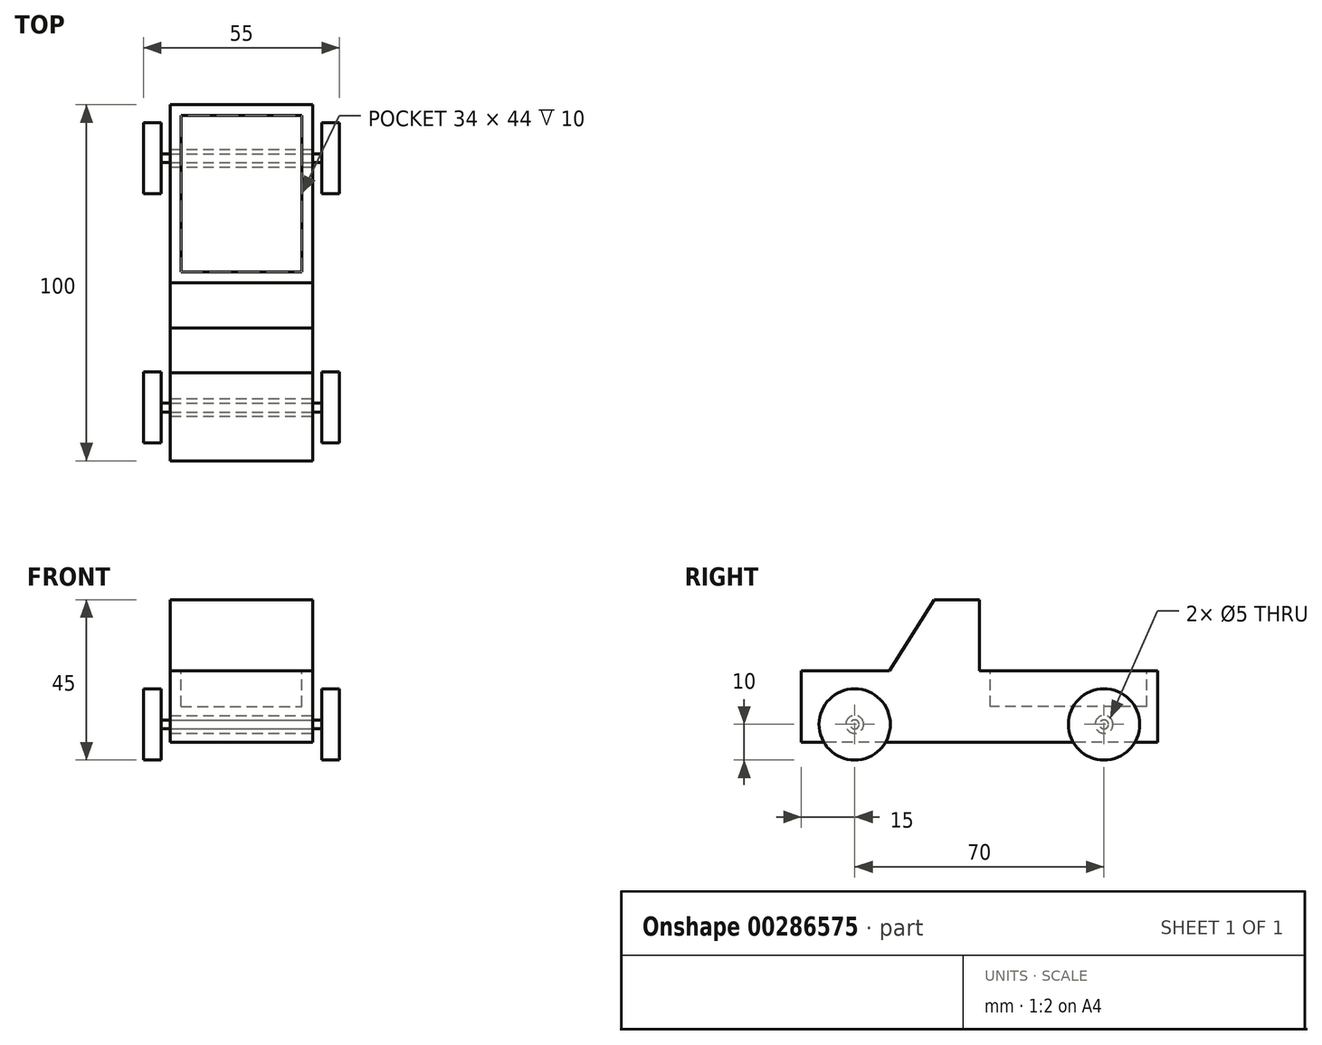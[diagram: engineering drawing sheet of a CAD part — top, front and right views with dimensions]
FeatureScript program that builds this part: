
annotation { "Feature Type Name" : "Feature", "Feature Type Description" : "" }
export const myFeature = defineFeature(function(context is Context, id is Id, definition is map)
    precondition{}
    {
        {
            var Q0;
            Q0=qCreatedBy(makeId("Right.planeOp"),FACE);
            var sketch = newSketch(context, id + "F0", { "sketchPlane" : qUnion([Q0])});
            skLineSegment(sketch, "E0.bottom", {"start": v(50, 10) * mm, "end": v(-50, 10) * mm});
            skLineSegment(sketch, "E0.top", {"start": v(50, -10) * mm, "end": v(-50, -10) * mm});
            skLineSegment(sketch, "E0.left", {"start": v(50, 10) * mm, "end": v(50, -10) * mm});
            skLineSegment(sketch, "E0.right", {"start": v(-50, 10) * mm, "end": v(-50, -10) * mm});
            skPoint(sketch, "E0.middle", {"position": v(0, 0) * mm});
            skSolve(sketch);
        }
        {
            var Q0;
            Q0 = qSketchRegion(id + "F0", true);
            extrude(context, id + "F1", {"entities" : qUnion([Q0]), "endBound" : BoundingType.SYMMETRIC, "depth" : 40 * mm});
        }
        {
            var Q0;
            Q0=makeQuery(id+"F1.opExtrude","SWEPT_FACE",FACE,{"disambiguationData":[OSD([sQuery(id+"F0.wireOp",EDGE,"E0.bottom")])]});
            var sketch = newSketch(context, id + "F2", { "sketchPlane" : qUnion([Q0])});
            skLineSegment(sketch, "E1", {"start": v(20, 0) * mm, "end": v(-20, 0) * mm});
            skSolve(sketch);
        }
        {
            var Q0;
            {var subQ0=sQuery(id+"F2.wireOp",EDGE,"E1");Q0=makeQuery(id+"F2.imprint","IMPRINT",FACE,{"disambiguationData":[TD([[makeQuery(id+"F2.imprint","IMPRINT",EDGE,{"derivedFrom":subQ0}),1.0]])]});}
            var sketch = newSketch(context, id + "F3", { "sketchPlane" : qUnion([Q0])});
            skLineSegment(sketch, "E2", {"start": v(-20, -25.3) * mm, "end": v(20, -25.3) * mm});
            skSolve(sketch);
        }
        {
            var Q0;
            {var subQ0=sQuery(id+"F3.wireOp",EDGE,"E2");Q0=makeQuery(id+"F3.imprint","IMPRINT",FACE,{"disambiguationData":[TD([[makeQuery(id+"F3.imprint","IMPRINT",EDGE,{"derivedFrom":subQ0}),1.0]])]});}
            var sketch = newSketch(context, id + "F4", { "sketchPlane" : qUnion([Q0])});
            skSolve(sketch);
        }
        {
            var Q0;
            Q0 = qSketchRegion(id + "F4", true);
            var Q1;
            {var subQ0=sQuery(id+"F3.wireOp",EDGE,"E2");Q1=makeQuery(id+"F4.imprint","IMPRINT",FACE,{"disambiguationData":[TD([[makeQuery(id+"F4.imprint","IMPRINT",EDGE,{"derivedFrom":makeQuery(id+"F3.imprint","IMPRINT",EDGE,{"derivedFrom":subQ0})}),1.0]])]});}
            extrude(context, id + "F5", {"entities" : qUnion([Q0, Q1]), "operationType" : NewBodyOperationType.ADD, "depth" : 20 * mm});
        }
        {
            var Q0;
            Q0=makeQuery(id+"F5.opExtrude","CAP_FACE",FACE,{"disambiguationData":[OSD([sQuery(id+"F0.wireOp",EDGE,"E0.bottom"),sQuery(id+"F2.wireOp",EDGE,"E1"),sQuery(id+"F3.wireOp",EDGE,"E2")])],"isStart":false});
            var sketch = newSketch(context, id + "F6", { "sketchPlane" : qUnion([Q0])});
            skLineSegment(sketch, "E3", {"start": v(-20, -15) * mm, "end": v(20, -15) * mm});
            skSolve(sketch);
        }
        {
            var Q0;
            {var subQ0=sQuery(id+"F0.wireOp",EDGE,"E0.bottom");var subQ1=makeQuery(id+"F1.opExtrude","CAP_EDGE",EDGE,{"disambiguationData":[OSD([subQ0])],"isStart":false});var subQ2=sQuery(id+"F0.wireOp",EDGE,"E0.right");var subQ3=sQuery(id+"F2.wireOp",EDGE,"E1");var subQ4=makeQuery(id+"F2.imprint","IMPRINT",EDGE,{"disambiguationData":[TD([[makeQuery(id+"F2.imprint","INTERSECT",VERTEX,{"derivedFrom":[subQ1,subQ3]}),-1.0]])],"derivedFrom":subQ1});Q0=makeQuery(id+"F5.boolean.opBoolean","MERGE",FACE,{"derivedFrom":[makeQuery(id+"F1.opExtrude","CAP_FACE",FACE,{"disambiguationData":[OSD([subQ0,sQuery(id+"F0.wireOp",EDGE,"E0.top"),sQuery(id+"F0.wireOp",EDGE,"E0.left"),subQ2])],"isStart":false}),makeQuery(id+"F5.opExtrude","SWEPT_FACE",FACE,{"disambiguationData":[OSD([subQ0]),TDD([makeQuery(id+"F4.imprint","IMPRINT",EDGE,{"derivedFrom":makeQuery(id+"F3.imprint","IMPRINT",EDGE,{"disambiguationData":[TD([[makeQuery(id+"F3.imprint","INTERSECT",VERTEX,{"derivedFrom":[makeQuery(id+"F2.imprint","IMPRINT",EDGE,{"derivedFrom":subQ3}),subQ4]}),-1.0]])],"derivedFrom":subQ4})})])]})]});}
            var sketch = newSketch(context, id + "F7", { "sketchPlane" : qUnion([Q0])});
            skLineSegment(sketch, "E4", {"start": v(-25.3, 10) * mm, "end": v(-12.65, 30) * mm});
            skSolve(sketch);
        }
        {
            var Q0;
            Q0=qCreatedBy(makeId("Right.planeOp"),FACE);
            var sketch = newSketch(context, id + "F8", { "sketchPlane" : qUnion([Q0])});
            skSolve(sketch);
        }
        {
            var Q0;
            Q0 = qSketchRegion(id + "F8", true);
            var Q1;
            {var subQ0=sQuery(id+"F7.wireOp",EDGE,"E4");Q1=makeQuery(id+"F7.imprint","IMPRINT",FACE,{"disambiguationData":[TD([[makeQuery(id+"F7.imprint","IMPRINT",EDGE,{"derivedFrom":subQ0}),1.0]])]});}
            extrude(context, id + "F9", {"entities" : qUnion([Q0, Q1]), "operationType" : NewBodyOperationType.REMOVE, "oppositeDirection" : true, "depth" : 40 * mm});
        }
        {
            var Q0;
            {var subQ0=sQuery(id+"F0.wireOp",EDGE,"E0.bottom");var subQ1=makeQuery(id+"F1.opExtrude","CAP_EDGE",EDGE,{"disambiguationData":[OSD([subQ0])],"isStart":false});var subQ2=sQuery(id+"F0.wireOp",EDGE,"E0.right");var subQ3=sQuery(id+"F2.wireOp",EDGE,"E1");var subQ4=makeQuery(id+"F2.imprint","IMPRINT",EDGE,{"disambiguationData":[TD([[makeQuery(id+"F2.imprint","INTERSECT",VERTEX,{"derivedFrom":[subQ1,subQ3]}),-1.0]])],"derivedFrom":subQ1});Q0=makeQuery(id+"F5.boolean.opBoolean","MERGE",FACE,{"derivedFrom":[makeQuery(id+"F1.opExtrude","CAP_FACE",FACE,{"disambiguationData":[OSD([subQ0,sQuery(id+"F0.wireOp",EDGE,"E0.top"),sQuery(id+"F0.wireOp",EDGE,"E0.left"),subQ2])],"isStart":false}),makeQuery(id+"F5.opExtrude","SWEPT_FACE",FACE,{"disambiguationData":[OSD([subQ0]),TDD([makeQuery(id+"F4.imprint","IMPRINT",EDGE,{"derivedFrom":makeQuery(id+"F3.imprint","IMPRINT",EDGE,{"disambiguationData":[TD([[makeQuery(id+"F3.imprint","INTERSECT",VERTEX,{"derivedFrom":[makeQuery(id+"F2.imprint","IMPRINT",EDGE,{"derivedFrom":subQ3}),subQ4]}),-1.0]])],"derivedFrom":subQ4})})])]})]});}
            var sketch = newSketch(context, id + "F10", { "sketchPlane" : qUnion([Q0])});
            skCircle(sketch, "E5", {"center": v(-35, -5) * mm, "radius": 2.5 * mm});
            skSolve(sketch);
        }
        {
            var Q0;
            Q0 = qSketchRegion(id + "F10", true);
            extrude(context, id + "F11", {"entities" : qUnion([Q0]), "operationType" : NewBodyOperationType.REMOVE, "endBound" : BoundingType.THROUGH_ALL, "oppositeDirection" : true, "depth" : 40 * mm});
        }
        {
            var Q0;
            {var subQ0=sQuery(id+"F0.wireOp",EDGE,"E0.bottom");var subQ1=makeQuery(id+"F1.opExtrude","CAP_EDGE",EDGE,{"disambiguationData":[OSD([subQ0])],"isStart":false});var subQ2=sQuery(id+"F0.wireOp",EDGE,"E0.right");var subQ3=sQuery(id+"F2.wireOp",EDGE,"E1");var subQ4=makeQuery(id+"F2.imprint","IMPRINT",EDGE,{"disambiguationData":[TD([[makeQuery(id+"F2.imprint","INTERSECT",VERTEX,{"derivedFrom":[subQ1,subQ3]}),-1.0]])],"derivedFrom":subQ1});Q0=makeQuery(id+"F5.boolean.opBoolean","MERGE",FACE,{"derivedFrom":[makeQuery(id+"F1.opExtrude","CAP_FACE",FACE,{"disambiguationData":[OSD([subQ0,sQuery(id+"F0.wireOp",EDGE,"E0.top"),sQuery(id+"F0.wireOp",EDGE,"E0.left"),subQ2])],"isStart":false}),makeQuery(id+"F5.opExtrude","SWEPT_FACE",FACE,{"disambiguationData":[OSD([subQ0]),TDD([makeQuery(id+"F4.imprint","IMPRINT",EDGE,{"derivedFrom":makeQuery(id+"F3.imprint","IMPRINT",EDGE,{"disambiguationData":[TD([[makeQuery(id+"F3.imprint","INTERSECT",VERTEX,{"derivedFrom":[makeQuery(id+"F2.imprint","IMPRINT",EDGE,{"derivedFrom":subQ3}),subQ4]}),-1.0]])],"derivedFrom":subQ4})})])]})]});}
            var sketch = newSketch(context, id + "F12", { "sketchPlane" : qUnion([Q0])});
            skCircle(sketch, "E6", {"center": v(35, -5) * mm, "radius": 2.5 * mm});
            skSolve(sketch);
        }
        {
            var Q0;
            Q0 = qSketchRegion(id + "F12", true);
            extrude(context, id + "F13", {"entities" : qUnion([Q0]), "operationType" : NewBodyOperationType.REMOVE, "endBound" : BoundingType.THROUGH_ALL, "oppositeDirection" : true, "depth" : 25 * mm});
        }
        {
            var Q0;
            {var subQ0=sQuery(id+"F2.wireOp",EDGE,"E1");Q0=makeQuery(id+"F2.imprint","IMPRINT",FACE,{"disambiguationData":[TD([[makeQuery(id+"F2.imprint","IMPRINT",EDGE,{"derivedFrom":subQ0}),-1.0]])]});}
            var sketch = newSketch(context, id + "F14", { "sketchPlane" : qUnion([Q0])});
            skLineSegment(sketch, "E7.0", {"start": v(-17, 3) * mm, "end": v(17, 3) * mm});
            skLineSegment(sketch, "E7.1", {"start": v(-17, 47) * mm, "end": v(-17, 3) * mm});
            skLineSegment(sketch, "E7.2", {"start": v(17, 47) * mm, "end": v(-17, 47) * mm});
            skLineSegment(sketch, "E7.3", {"start": v(17, 3) * mm, "end": v(17, 47) * mm});
            skSolve(sketch);
        }
        {
            var Q0;
            Q0 = qSketchRegion(id + "F14", true);
            extrude(context, id + "F15", {"entities" : qUnion([Q0]), "operationType" : NewBodyOperationType.REMOVE, "oppositeDirection" : true, "depth" : 10 * mm});
        }
        {
            var Q0;
            {var subQ0=sQuery(id+"F0.wireOp",EDGE,"E0.bottom");var subQ1=makeQuery(id+"F1.opExtrude","CAP_EDGE",EDGE,{"disambiguationData":[OSD([subQ0])],"isStart":false});var subQ2=sQuery(id+"F0.wireOp",EDGE,"E0.right");var subQ3=sQuery(id+"F2.wireOp",EDGE,"E1");var subQ4=makeQuery(id+"F2.imprint","IMPRINT",EDGE,{"disambiguationData":[TD([[makeQuery(id+"F2.imprint","INTERSECT",VERTEX,{"derivedFrom":[subQ1,subQ3]}),-1.0]])],"derivedFrom":subQ1});Q0=makeQuery(id+"F5.boolean.opBoolean","MERGE",FACE,{"derivedFrom":[makeQuery(id+"F1.opExtrude","CAP_FACE",FACE,{"disambiguationData":[OSD([subQ0,sQuery(id+"F0.wireOp",EDGE,"E0.top"),sQuery(id+"F0.wireOp",EDGE,"E0.left"),subQ2])],"isStart":false}),makeQuery(id+"F5.opExtrude","SWEPT_FACE",FACE,{"disambiguationData":[OSD([subQ0]),TDD([makeQuery(id+"F4.imprint","IMPRINT",EDGE,{"derivedFrom":makeQuery(id+"F3.imprint","IMPRINT",EDGE,{"disambiguationData":[TD([[makeQuery(id+"F3.imprint","INTERSECT",VERTEX,{"derivedFrom":[makeQuery(id+"F2.imprint","IMPRINT",EDGE,{"derivedFrom":subQ3}),subQ4]}),-1.0]])],"derivedFrom":subQ4})})])]})]});}
            var sketch = newSketch(context, id + "F16", { "sketchPlane" : qUnion([Q0])});
            skCircle(sketch, "E8", {"center": v(-35, -5) * mm, "radius": 1.25 * mm});
            skSolve(sketch);
        }
        {
            var Q0;
            Q0 = qSketchRegion(id + "F16", true);
            var Q1;
            Q1 = qSketchRegion(id + "F6", true);
            extrude(context, id + "F17", {"entities" : qUnion([Q0, Q1]), "operationType" : NewBodyOperationType.ADD, "oppositeDirection" : true, "depth" : 42.5 * mm});
        }
        {
            var Q0;
            Q0=makeQuery(id+"F17.opExtrude","CAP_FACE",FACE,{"disambiguationData":[OSD([sQuery(id+"F16.wireOp",EDGE,"E8")])],"isStart":true});
            extrude(context, id + "F18", {"entities" : qUnion([Q0]), "operationType" : NewBodyOperationType.ADD, "depth" : 2.5 * mm});
        }
        {
            var Q0;
            {var subQ0=sQuery(id+"F0.wireOp",EDGE,"E0.bottom");var subQ1=makeQuery(id+"F1.opExtrude","CAP_EDGE",EDGE,{"disambiguationData":[OSD([subQ0])],"isStart":false});var subQ2=sQuery(id+"F0.wireOp",EDGE,"E0.right");var subQ3=sQuery(id+"F2.wireOp",EDGE,"E1");var subQ4=makeQuery(id+"F2.imprint","IMPRINT",EDGE,{"disambiguationData":[TD([[makeQuery(id+"F2.imprint","INTERSECT",VERTEX,{"derivedFrom":[subQ1,subQ3]}),-1.0]])],"derivedFrom":subQ1});Q0=makeQuery(id+"F5.boolean.opBoolean","MERGE",FACE,{"derivedFrom":[makeQuery(id+"F1.opExtrude","CAP_FACE",FACE,{"disambiguationData":[OSD([subQ0,sQuery(id+"F0.wireOp",EDGE,"E0.top"),sQuery(id+"F0.wireOp",EDGE,"E0.left"),subQ2])],"isStart":false}),makeQuery(id+"F5.opExtrude","SWEPT_FACE",FACE,{"disambiguationData":[OSD([subQ0]),TDD([makeQuery(id+"F4.imprint","IMPRINT",EDGE,{"derivedFrom":makeQuery(id+"F3.imprint","IMPRINT",EDGE,{"disambiguationData":[TD([[makeQuery(id+"F3.imprint","INTERSECT",VERTEX,{"derivedFrom":[makeQuery(id+"F2.imprint","IMPRINT",EDGE,{"derivedFrom":subQ3}),subQ4]}),-1.0]])],"derivedFrom":subQ4})})])]})]});}
            var sketch = newSketch(context, id + "F19", { "sketchPlane" : qUnion([Q0])});
            skCircle(sketch, "E9", {"center": v(35, -5) * mm, "radius": 1.25 * mm});
            skSolve(sketch);
        }
        {
            var Q0;
            Q0 = qSketchRegion(id + "F19", true);
            extrude(context, id + "F20", {"entities" : qUnion([Q0]), "operationType" : NewBodyOperationType.ADD, "oppositeDirection" : true, "depth" : 42.5 * mm});
        }
        {
            var Q0;
            Q0=makeQuery(id+"F20.opExtrude","CAP_FACE",FACE,{"disambiguationData":[OSD([sQuery(id+"F19.wireOp",EDGE,"E9")])],"isStart":true});
            extrude(context, id + "F21", {"entities" : qUnion([Q0]), "operationType" : NewBodyOperationType.ADD, "depth" : 2.5 * mm});
        }
        {
            var Q0;
            Q0=makeQuery(id+"F18.opExtrude","CAP_FACE",FACE,{"disambiguationData":[OSD([sQuery(id+"F16.wireOp",EDGE,"E8")])],"isStart":false});
            var sketch = newSketch(context, id + "F22", { "sketchPlane" : qUnion([Q0])});
            skCircle(sketch, "E10", {"center": v(-35, -5) * mm, "radius": 10 * mm});
            skSolve(sketch);
        }
        {
            var Q0;
            Q0 = qSketchRegion(id + "F22", true);
            extrude(context, id + "F23", {"entities" : qUnion([Q0]), "operationType" : NewBodyOperationType.ADD, "depth" : 5 * mm});
        }
        {
            var Q0;
            Q0=makeQuery(id+"F17.opExtrude","CAP_FACE",FACE,{"disambiguationData":[OSD([sQuery(id+"F16.wireOp",EDGE,"E8")])],"isStart":false});
            var sketch = newSketch(context, id + "F24", { "sketchPlane" : qUnion([Q0])});
            skCircle(sketch, "E11", {"center": v(35, -5) * mm, "radius": 10 * mm});
            skSolve(sketch);
        }
        {
            var Q0;
            Q0 = qSketchRegion(id + "F24", true);
            extrude(context, id + "F25", {"entities" : qUnion([Q0]), "operationType" : NewBodyOperationType.ADD, "depth" : 5 * mm});
        }
        {
            var Q0;
            Q0=makeQuery(id+"F20.opExtrude","CAP_FACE",FACE,{"disambiguationData":[OSD([sQuery(id+"F19.wireOp",EDGE,"E9")])],"isStart":false});
            var sketch = newSketch(context, id + "F26", { "sketchPlane" : qUnion([Q0])});
            skCircle(sketch, "E12", {"center": v(-35, -5) * mm, "radius": 10 * mm});
            skSolve(sketch);
        }
        {
            var Q0;
            Q0 = qSketchRegion(id + "F26", true);
            extrude(context, id + "F27", {"entities" : qUnion([Q0]), "operationType" : NewBodyOperationType.ADD, "depth" : 5 * mm});
        }
        {
            var Q0;
            Q0=makeQuery(id+"F21.opExtrude","CAP_FACE",FACE,{"disambiguationData":[OSD([sQuery(id+"F19.wireOp",EDGE,"E9")])],"isStart":false});
            var sketch = newSketch(context, id + "F28", { "sketchPlane" : qUnion([Q0])});
            skCircle(sketch, "E13", {"center": v(35, -5) * mm, "radius": 10 * mm});
            skSolve(sketch);
        }
        {
            var Q0;
            Q0 = qSketchRegion(id + "F28", true);
            extrude(context, id + "F29", {"entities" : qUnion([Q0]), "operationType" : NewBodyOperationType.ADD, "depth" : 5 * mm});
        }
    });
